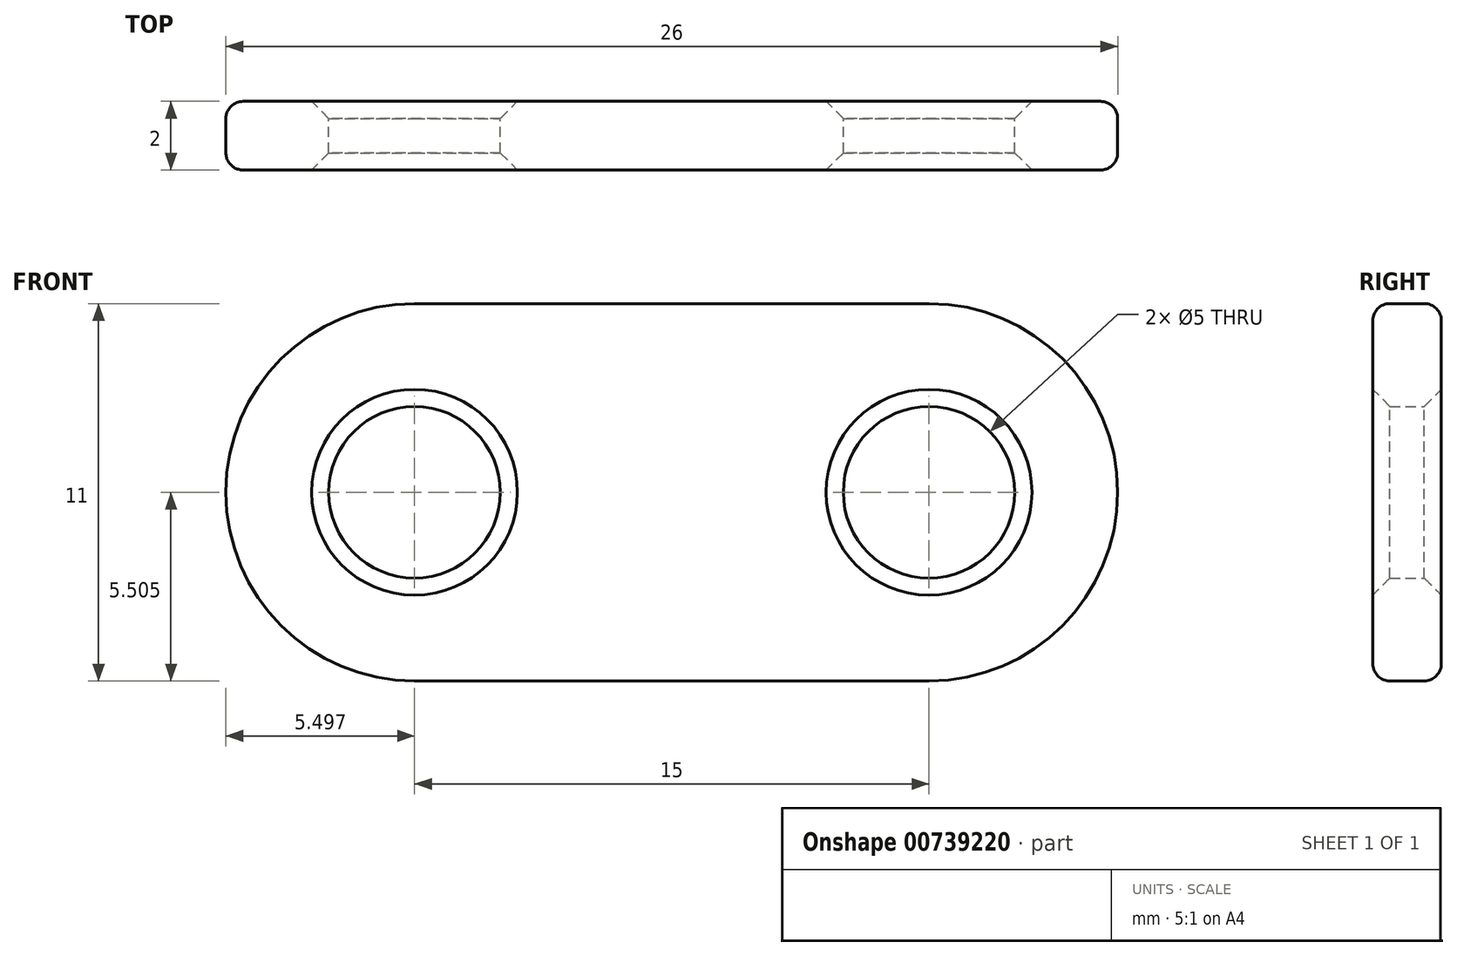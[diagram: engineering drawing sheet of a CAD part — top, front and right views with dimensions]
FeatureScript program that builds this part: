
annotation { "Feature Type Name" : "Feature", "Feature Type Description" : "" }
export const myFeature = defineFeature(function(context is Context, id is Id, definition is map)
    precondition{}
    {
        {
            var Q0;
            Q0=qCreatedBy(makeId("Front.planeOp"),FACE);
            var sketch = newSketch(context, id + "F0", { "sketchPlane" : qUnion([Q0])});
            skLineSegment(sketch, "E0", {"start": v(-6.04, 9.61) * mm, "end": v(8.96, 9.61) * mm});
            skLineSegment(sketch, "E1", {"start": v(-6.04, -1.39) * mm, "end": v(8.96, -1.39) * mm});
            skArc(sketch, "E2", {"start": v(-6.04, 9.61) * mm, "mid": v(-11.54, 4.11) * mm, "end": v(-6.04, -1.39) * mm});
            skArc(sketch, "E3", {"start": v(8.96, -1.39) * mm, "mid": v(14.46, 4.11) * mm, "end": v(8.96, 9.61) * mm});
            skCircle(sketch, "E4", {"center": v(-6.04, 4.11) * mm, "radius": 2.5 * mm});
            skCircle(sketch, "E5", {"center": v(8.96, 4.11) * mm, "radius": 2.5 * mm});
            skSolve(sketch);
        }
        {
            var Q0;
            Q0 = qSketchRegion(id + "F0", true);
            extrude(context, id + "F1", {"entities" : qUnion([Q0]), "depth" : 2 * mm, "offsetDistance" : 25.4 * mm});
        }
        {
            var Q0;
            Q0=makeQuery(id+"F1.opExtrude","CAP_EDGE",EDGE,{"disambiguationData":[OSD([sQuery(id+"F0.wireOp",EDGE,"E4")])],"isStart":false});
            var Q1;
            Q1=makeQuery(id+"F1.opExtrude","CAP_EDGE",EDGE,{"disambiguationData":[OSD([sQuery(id+"F0.wireOp",EDGE,"E5")])],"isStart":false});
            var Q2;
            Q2=makeQuery(id+"F1.opExtrude","CAP_EDGE",EDGE,{"disambiguationData":[OSD([sQuery(id+"F0.wireOp",EDGE,"E4")])],"isStart":true});
            var Q3;
            Q3=makeQuery(id+"F1.opExtrude","CAP_EDGE",EDGE,{"disambiguationData":[OSD([sQuery(id+"F0.wireOp",EDGE,"E5")])],"isStart":true});
            chamfer(context, id + "F2", {"entities" : qUnion([Q0, Q1, Q2, Q3]), "width" : 0.5 * mm, "tangentPropagation" : true});
        }
        {
            var Q0;
            Q0=makeQuery(id+"F1.opExtrude","CAP_EDGE",EDGE,{"disambiguationData":[OSD([sQuery(id+"F0.wireOp",EDGE,"E1")])],"isStart":false});
            var Q1;
            Q1=makeQuery(id+"F1.opExtrude","CAP_EDGE",EDGE,{"disambiguationData":[OSD([sQuery(id+"F0.wireOp",EDGE,"E1")])],"isStart":true});
            fillet(context, id + "F3", {"entities" : qUnion([Q0, Q1]), "radius" : 0.5 * mm, "tangentPropagation" : true, "allowEdgeOverflow" : false});
        }
    });
